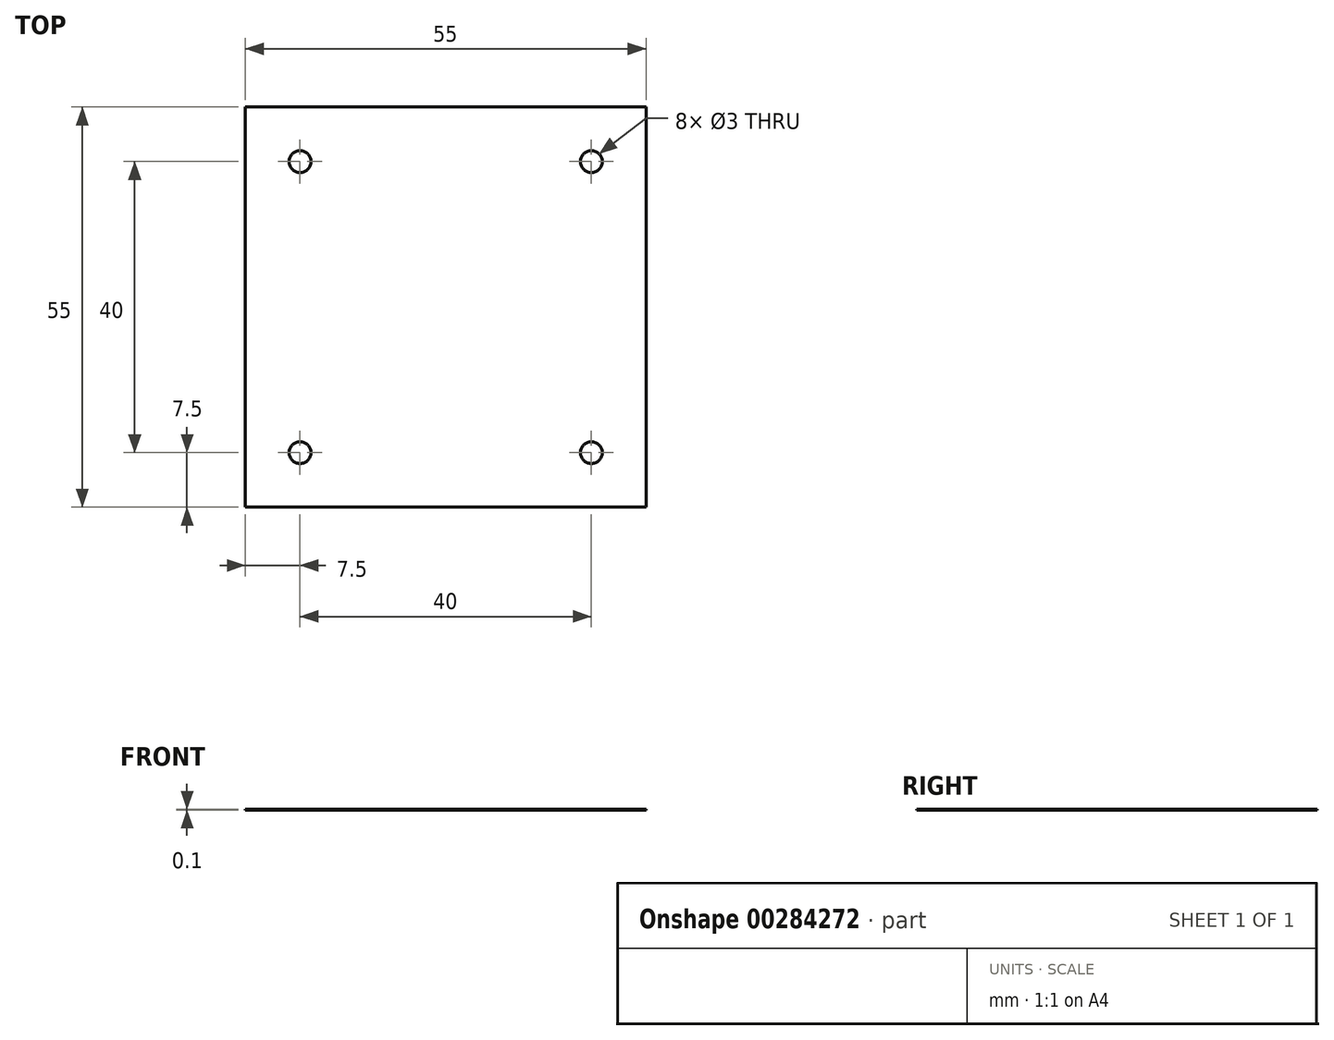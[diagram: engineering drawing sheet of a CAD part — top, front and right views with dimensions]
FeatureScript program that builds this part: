
annotation { "Feature Type Name" : "Feature", "Feature Type Description" : "" }
export const myFeature = defineFeature(function(context is Context, id is Id, definition is map)
    precondition{}
    {
        {
            var Q0;
            Q0=qCreatedBy(makeId("Top.planeOp"),FACE);
            var sketch = newSketch(context, id + "F0", { "sketchPlane" : qUnion([Q0])});
            skCircle(sketch, "E0", {"center": v(-20, -20) * mm, "radius": 1.5 * mm});
            skCircle(sketch, "E1.0.1.0", {"center": v(-20, 20) * mm, "radius": 1.5 * mm});
            skCircle(sketch, "E1.1.0.0", {"center": v(20, -20) * mm, "radius": 1.5 * mm});
            skCircle(sketch, "E1.1.1.0", {"center": v(20, 20) * mm, "radius": 1.5 * mm});
            skLineSegment(sketch, "E1.direction1", {"start": v(-20, -20) * mm, "end": v(20, -20) * mm, "construction": true});
            skLineSegment(sketch, "E1.direction2", {"start": v(-20, -20) * mm, "end": v(-20, 20) * mm, "construction": true});
            skLineSegment(sketch, "E2.bottom", {"start": v(27.5, 27.5) * mm, "end": v(-27.5, 27.5) * mm});
            skLineSegment(sketch, "E2.top", {"start": v(27.5, -27.5) * mm, "end": v(-27.5, -27.5) * mm});
            skLineSegment(sketch, "E2.left", {"start": v(27.5, 27.5) * mm, "end": v(27.5, -27.5) * mm});
            skLineSegment(sketch, "E2.right", {"start": v(-27.5, 27.5) * mm, "end": v(-27.5, -27.5) * mm});
            skPoint(sketch, "E2.middle", {"position": v(0, 0) * mm});
            skSolve(sketch);
        }
        {
            var Q0;
            Q0=makeQuery(id+"F0.imprint","IMPRINT",FACE,{"disambiguationData":[TD([[makeQuery(id+"F0.imprint","IMPRINT",EDGE,{"derivedFrom":sQuery(id+"F0.wireOp",EDGE,"E0")}),-1.0]])]});
            extrude(context, id + "F1", {"entities" : qUnion([Q0]), "depth" : .1 * mm});
        }
    });
